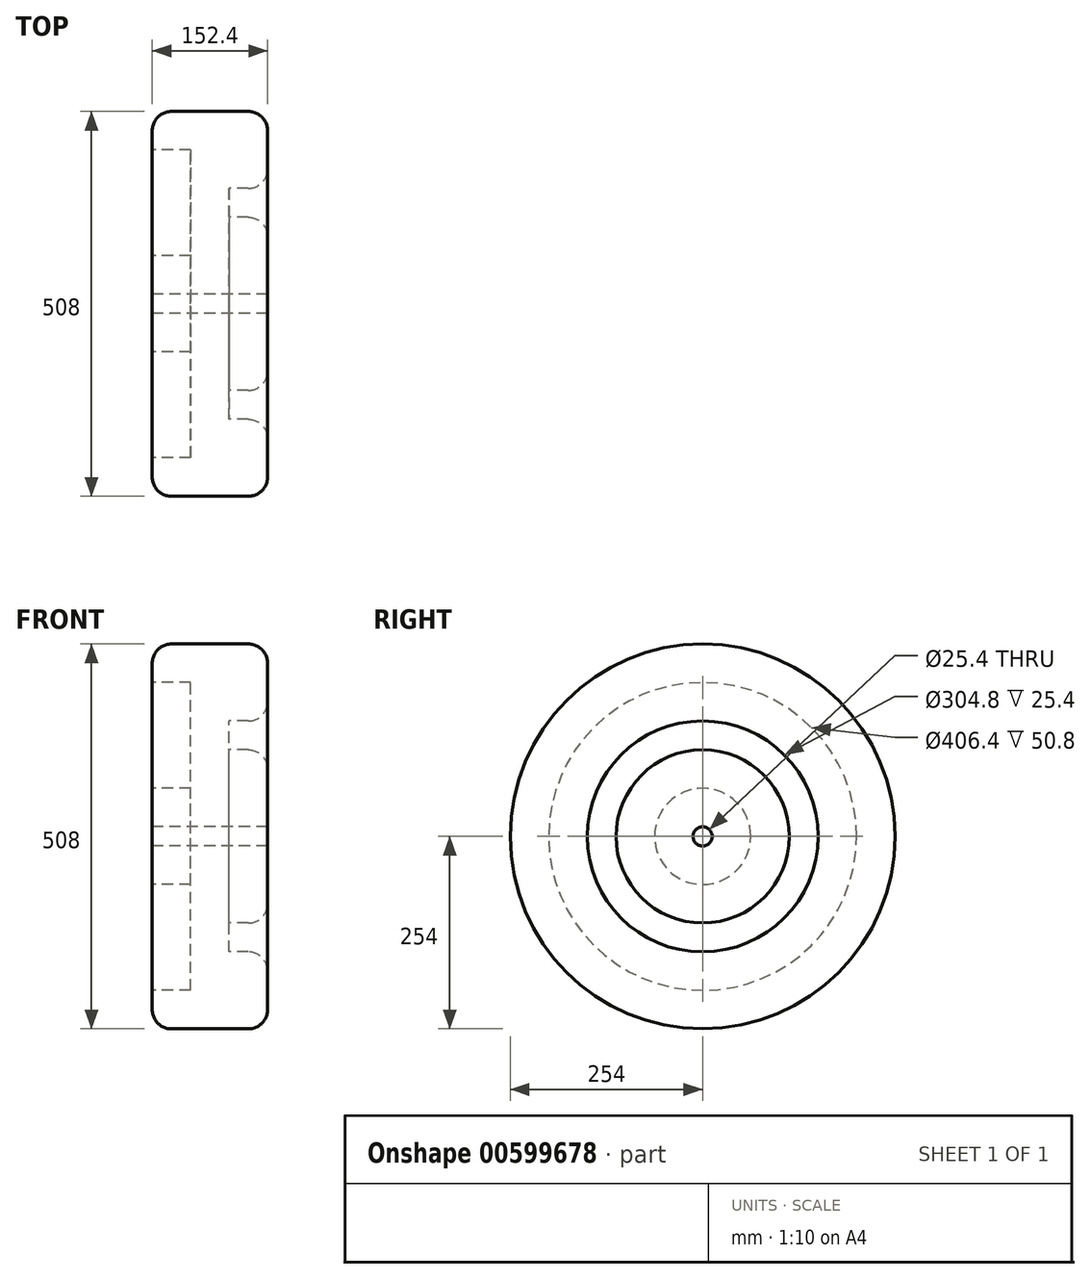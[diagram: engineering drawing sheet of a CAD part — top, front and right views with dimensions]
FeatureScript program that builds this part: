
annotation { "Feature Type Name" : "Feature", "Feature Type Description" : "" }
export const myFeature = defineFeature(function(context is Context, id is Id, definition is map)
    precondition{}
    {
        {
            var Q0;
            Q0=qCreatedBy(makeId("Right.planeOp"),FACE);
            var sketch = newSketch(context, id + "F0", { "sketchPlane" : qUnion([Q0])});
            skCircle(sketch, "E0", {"center": v(0, 0) * mm, "radius": 12.7 * mm});
            skCircle(sketch, "E1", {"center": v(0, 0) * mm, "radius": 254 * mm});
            skSolve(sketch);
        }
        {
            var Q0;
            Q0=makeQuery(id+"F0.imprint","IMPRINT",FACE,{"disambiguationData":[TD([[makeQuery(id+"F0.imprint","IMPRINT",EDGE,{"derivedFrom":sQuery(id+"F0.wireOp",EDGE,"E0")}),-1.0]])]});
            extrude(context, id + "F1", {"entities" : qUnion([Q0]), "depth" : 152.4 * mm, "offsetDistance" : 25.4 * mm});
        }
        {
            var Q0;
            Q0=makeQuery(id+"F1.opExtrude","CAP_FACE",FACE,{"disambiguationData":[OSD([sQuery(id+"F0.wireOp",EDGE,"E0"),sQuery(id+"F0.wireOp",EDGE,"E1")])],"isStart":false});
            shell(context, id + "F2", {"entities" : qUnion([Q0]), "thickness" : 101.6 * mm});
        }
        {
            var Q0;
            {var subQ0=sQuery(id+"F0.wireOp",EDGE,"E1");Q0=makeQuery(id+"F2.opShell","OFFSET_EDGE",EDGE,{"disambiguationData":[OSD([subQ0]),TDD([makeQuery(id+"F1.opExtrude","CAP_EDGE",EDGE,{"disambiguationData":[OSD([subQ0])],"isStart":false})])]});}
            fillet(context, id + "F3", {"entities" : qUnion([Q0]), "radius" : 25.4 * mm, "tangentPropagation" : true, "allowEdgeOverflow" : false});
        }
        {
            var Q0;
            Q0=makeQuery(id+"F1.opExtrude","CAP_EDGE",EDGE,{"disambiguationData":[OSD([sQuery(id+"F0.wireOp",EDGE,"E1")])],"isStart":false});
            var Q1;
            Q1=makeQuery(id+"F1.opExtrude","CAP_EDGE",EDGE,{"disambiguationData":[OSD([sQuery(id+"F0.wireOp",EDGE,"E1")])],"isStart":true});
            fillet(context, id + "F4", {"entities" : qUnion([Q0, Q1]), "radius" : 25.4 * mm, "tangentPropagation" : true, "allowEdgeOverflow" : false});
        }
        {
            var Q0;
            Q0=makeQuery(id+"F1.opExtrude","CAP_FACE",FACE,{"disambiguationData":[OSD([sQuery(id+"F0.wireOp",EDGE,"E0"),sQuery(id+"F0.wireOp",EDGE,"E1")])],"isStart":true});
            shell(context, id + "F5", {"entities" : qUnion([Q0]), "thickness" : 50.8 * mm});
        }
        {
            var Q0;
            {var subQ0=sQuery(id+"F0.wireOp",EDGE,"E0");Q0=makeQuery(id+"F2.opShell","OFFSET_EDGE",EDGE,{"disambiguationData":[OSD([subQ0]),TDD([makeQuery(id+"F1.opExtrude","CAP_EDGE",EDGE,{"disambiguationData":[OSD([subQ0])],"isStart":false})])]});}
            fillet(context, id + "F6", {"entities" : qUnion([Q0]), "radius" : 25.4 * mm, "tangentPropagation" : true, "allowEdgeOverflow" : false});
        }
    });
